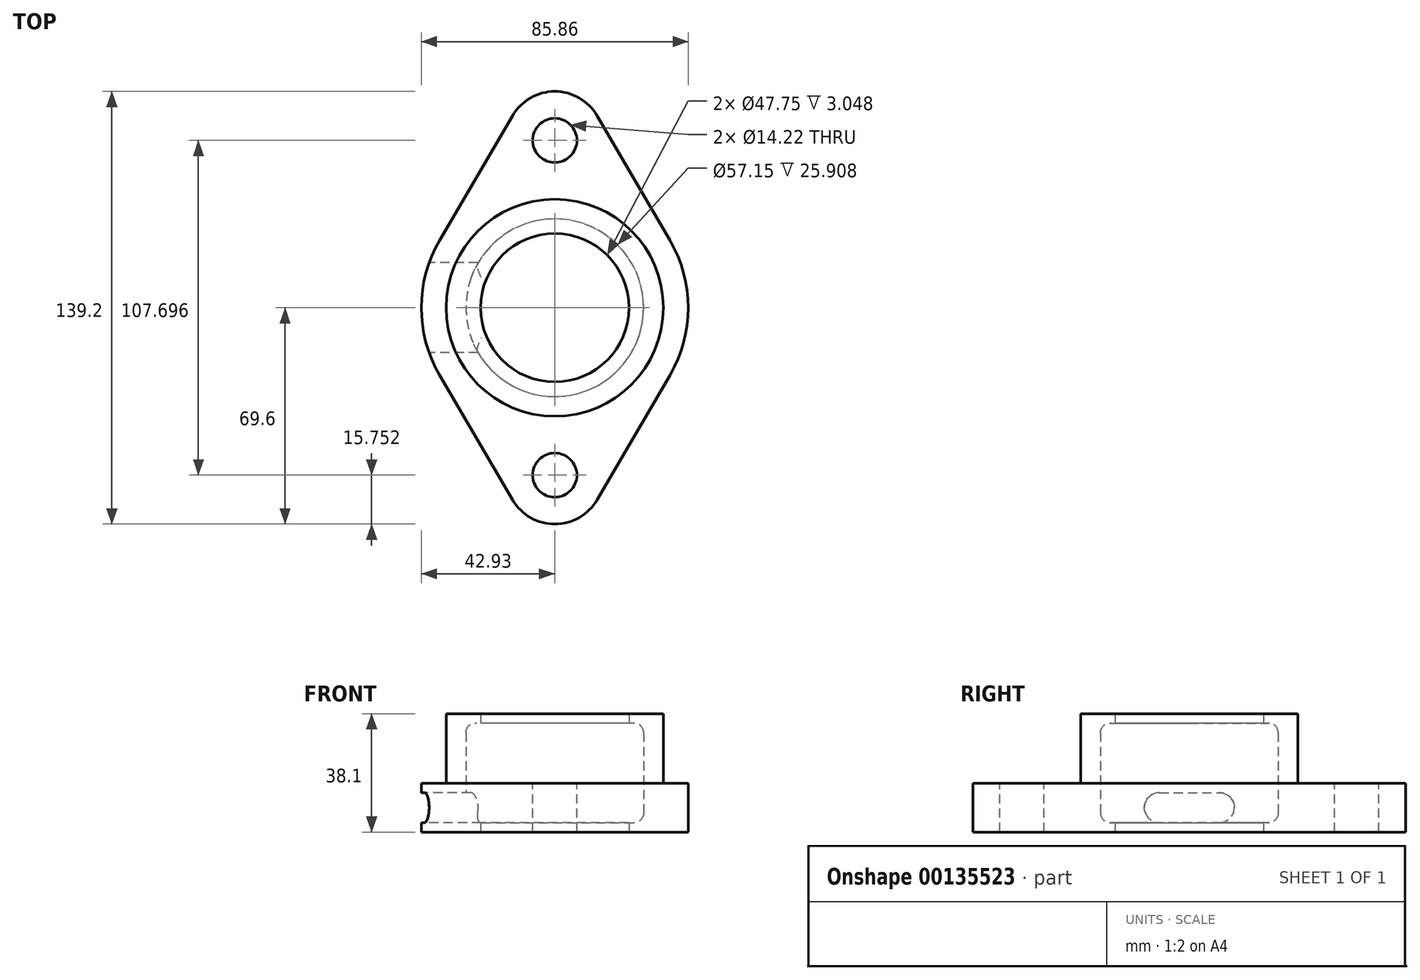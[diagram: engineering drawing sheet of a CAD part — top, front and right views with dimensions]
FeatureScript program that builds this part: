
annotation { "Feature Type Name" : "Feature", "Feature Type Description" : "" }
export const myFeature = defineFeature(function(context is Context, id is Id, definition is map)
    precondition{}
    {
        {
            var Q0;
            Q0=qCreatedBy(makeId("Top.planeOp"),FACE);
            var sketch = newSketch(context, id + "F0", { "sketchPlane" : qUnion([Q0])});
            skCircle(sketch, "E0", {"center": v(0, 0) * mm, "radius": 28.58 * mm});
            skCircle(sketch, "E1", {"center": v(0, 0) * mm, "radius": 34.93 * mm});
            skCircle(sketch, "E2", {"center": v(0, 0) * mm, "radius": 23.88 * mm});
            skSolve(sketch);
        }
        {
            var Q0;
            Q0=makeQuery(id+"F0.imprint","IMPRINT",FACE,{"disambiguationData":[TD([[makeQuery(id+"F0.imprint","IMPRINT",EDGE,{"derivedFrom":sQuery(id+"F0.wireOp",EDGE,"E2")}),1.0]])]});
            var Q1;
            Q1=makeQuery(id+"F0.imprint","IMPRINT",FACE,{"disambiguationData":[TD([[makeQuery(id+"F0.imprint","IMPRINT",EDGE,{"derivedFrom":sQuery(id+"F0.wireOp",EDGE,"E0")}),1.0]])]});
            var Q2;
            Q2=makeQuery(id+"F0.imprint","IMPRINT",FACE,{"disambiguationData":[TD([[makeQuery(id+"F0.imprint","IMPRINT",EDGE,{"derivedFrom":sQuery(id+"F0.wireOp",EDGE,"E0")}),-1.0]])]});
            extrude(context, id + "F1", {"entities" : qUnion([Q0, Q1, Q2]), "endBound" : BoundingType.SYMMETRIC, "depth" : 38.1 * mm});
        }
        {
            var Q0;
            Q0=makeQuery(id+"F0.imprint","IMPRINT",FACE,{"disambiguationData":[TD([[makeQuery(id+"F0.imprint","IMPRINT",EDGE,{"derivedFrom":sQuery(id+"F0.wireOp",EDGE,"E0")}),1.0]])]});
            var Q1;
            Q1=makeQuery(id+"F0.imprint","IMPRINT",FACE,{"disambiguationData":[TD([[makeQuery(id+"F0.imprint","IMPRINT",EDGE,{"derivedFrom":sQuery(id+"F0.wireOp",EDGE,"E2")}),1.0]])]});
            extrude(context, id + "F2", {"entities" : qUnion([Q0, Q1]), "operationType" : NewBodyOperationType.REMOVE, "endBound" : BoundingType.SYMMETRIC, "depth" : 32 * mm});
        }
        {
            var Q0;
            Q0=makeQuery(id+"F0.imprint","IMPRINT",FACE,{"disambiguationData":[TD([[makeQuery(id+"F0.imprint","IMPRINT",EDGE,{"derivedFrom":sQuery(id+"F0.wireOp",EDGE,"E2")}),1.0]])]});
            extrude(context, id + "F3", {"entities" : qUnion([Q0]), "operationType" : NewBodyOperationType.REMOVE, "endBound" : BoundingType.THROUGH_ALL, "depth" : 25.4 * mm, "hasSecondDirection" : true, "secondDirectionBound" : SecondDirectionBoundingType.THROUGH_ALL, "secondDirectionOppositeDirection" : true, "secondDirectionDepth" : 25.4 * mm});
        }
        {
            var Q0;
            Q0=makeQuery(id+"F2.boolean.opBoolean","COPY",EDGE,{"derivedFrom":makeQuery(id+"F2.opExtrude","CAP_EDGE",EDGE,{"disambiguationData":[OSD([sQuery(id+"F0.wireOp",EDGE,"E0")])],"isStart":true})});
            var Q1;
            Q1=makeQuery(id+"F2.boolean.opBoolean","COPY",EDGE,{"derivedFrom":makeQuery(id+"F2.opExtrude","CAP_EDGE",EDGE,{"disambiguationData":[OSD([sQuery(id+"F0.wireOp",EDGE,"E0")])],"isStart":false})});
            fillet(context, id + "F4", {"entities" : qUnion([Q0, Q1]), "radius" : 3.05 * mm, "tangentPropagation" : true, "allowEdgeOverflow" : false});
        }
        {
            var Q0;
            Q0=makeQuery(id+"F1.opExtrude","CAP_FACE",FACE,{"disambiguationData":[OSD([sQuery(id+"F0.wireOp",EDGE,"E1")])],"isStart":false});
            var sketch = newSketch(context, id + "F5", { "sketchPlane" : qUnion([Q0])});
            skCircle(sketch, "E3", {"center": v(0, 53.85) * mm, "radius": 7.11 * mm});
            skCircle(sketch, "E4.MirrorC", {"center": v(0, -53.85) * mm, "radius": 7.11 * mm});
            skCircle(sketch, "E5", {"center": v(0, 0) * mm, "radius": 42.93 * mm});
            skArc(sketch, "E6", {"start": v(13.6, 61.8) * mm, "mid": v(0, 69.6) * mm, "end": v(-13.6, 61.8) * mm});
            skLineSegment(sketch, "E7", {"start": v(13.6, 61.8) * mm, "end": v(37.06, 21.67) * mm});
            skLineSegment(sketch, "E8", {"start": v(-13.6, 61.8) * mm, "end": v(-37.06, 21.67) * mm});
            skLineSegment(sketch, "E9.MirrorCS", {"start": v(13.6, -61.8) * mm, "end": v(37.06, -21.67) * mm});
            skArc(sketch, "E10.MirrorCS", {"start": v(13.6, -61.8) * mm, "mid": v(0, -69.6) * mm, "end": v(-13.6, -61.8) * mm});
            skLineSegment(sketch, "E11.MirrorCS", {"start": v(-13.6, -61.8) * mm, "end": v(-37.06, -21.67) * mm});
            skCircle(sketch, "E12.0", {"center": v(0, 0) * mm, "radius": 34.93 * mm});
            skSolve(sketch);
        }
        {
            var Q0;
            Q0 = qSketchRegion(id + "F5", true);
            extrude(context, id + "F6", {"entities" : qUnion([Q0]), "operationType" : NewBodyOperationType.ADD, "oppositeDirection" : true, "depth" : 38.1 * mm, "hasSecondDirection" : true, "secondDirectionOppositeDirection" : true, "secondDirectionDepth" : 22.35 * mm});
        }
        {
            var Q0;
            Q0=qCreatedBy(makeId("Right.planeOp"),FACE);
            cPlane(context, id + "F7", {"entities" : qUnion([Q0]), "cplaneType" : CPlaneType.OFFSET, "offset" : 42.93 * mm, "oppositeDirection" : true, "width" : 152.4 * mm, "height" : 152.4 * mm});
        }
        {
            var Q0;
            Q0=qCreatedBy(id+"F7.planeOp",FACE);
            var sketch = newSketch(context, id + "F8", { "sketchPlane" : qUnion([Q0])});
            skLineSegment(sketch, "E13.0", {"start": v(-61.8, -19.05) * mm, "end": v(-21.67, -19.05) * mm, "construction": true});
            skLineSegment(sketch, "E14.0", {"start": v(21.67, -19.05) * mm, "end": v(-21.67, -19.05) * mm, "construction": true});
            skLineSegment(sketch, "E15", {"start": v(0, -19.05) * mm, "end": v(0, -11.18) * mm, "construction": true});
            skLineSegment(sketch, "E16", {"start": v(9.65, -11.18) * mm, "end": v(-9.65, -11.18) * mm, "construction": true});
            skArc(sketch, "E17.0.startCap", {"start": v(9.65, -6.35) * mm, "mid": v(14.48, -11.18) * mm, "end": v(9.65, -16) * mm});
            skArc(sketch, "E17.0.endCap", {"start": v(-9.65, -16) * mm, "mid": v(-14.48, -11.18) * mm, "end": v(-9.65, -6.35) * mm});
            skLineSegment(sketch, "E17.0.left", {"start": v(9.65, -16) * mm, "end": v(-9.65, -16) * mm});
            skLineSegment(sketch, "E17.0.right", {"start": v(9.65, -6.35) * mm, "end": v(-9.65, -6.35) * mm});
            skSolve(sketch);
        }
        {
            var Q0;
            Q0 = qSketchRegion(id + "F8", true);
            extrude(context, id + "F9", {"entities" : qUnion([Q0]), "operationType" : NewBodyOperationType.REMOVE, "depth" : 25.4 * mm});
        }
    });
